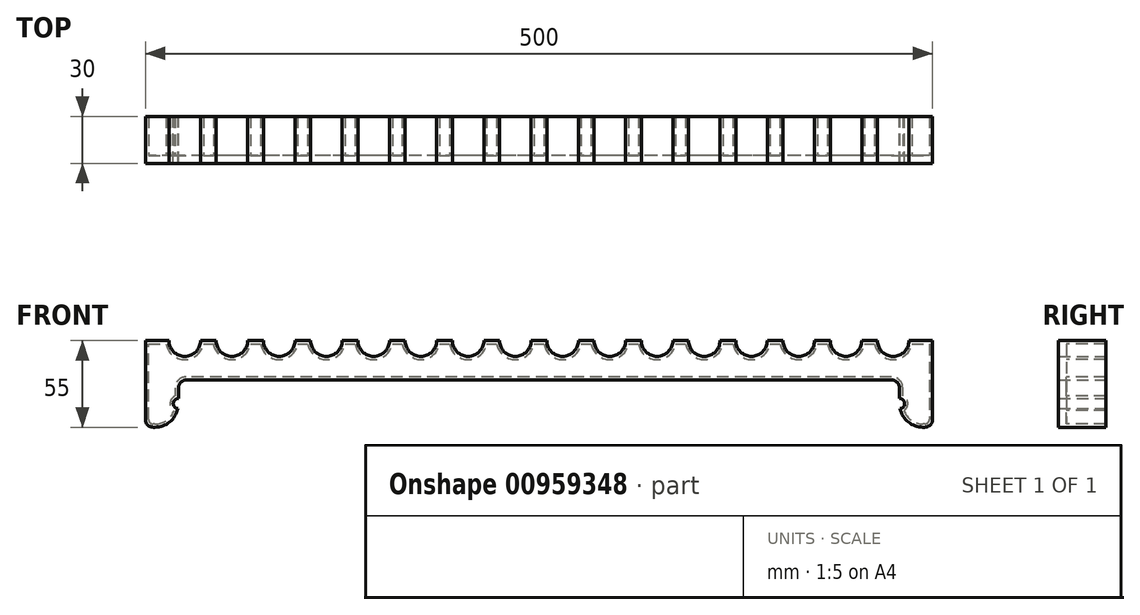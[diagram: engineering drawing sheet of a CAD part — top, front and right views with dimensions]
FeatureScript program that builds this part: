
annotation { "Feature Type Name" : "Feature", "Feature Type Description" : "" }
export const myFeature = defineFeature(function(context is Context, id is Id, definition is map)
    precondition{}
    {
        {
            var Q0;
            Q0=qCreatedBy(makeId("Front.planeOp"),FACE);
            var sketch = newSketch(context, id + "F0", { "sketchPlane" : qUnion([Q0])});
            skLineSegment(sketch, "E0.bottom", {"start": v(5, 0) * mm, "end": v(6, 0) * mm});
            skLineSegment(sketch, "E0.top", {"start": v(0, 55) * mm, "end": v(15, 55) * mm});
            skLineSegment(sketch, "E0.left", {"start": v(0, 5) * mm, "end": v(0, 55) * mm});
            skLineSegment(sketch, "E0.right", {"start": v(500, 5) * mm, "end": v(500, 55) * mm});
            skLineSegment(sketch, "E1.top", {"start": v(26, 30) * mm, "end": v(474, 30) * mm});
            skArc(sketch, "E2", {"start": v(15, 55) * mm, "mid": v(25, 45) * mm, "end": v(35, 55) * mm});
            skLineSegment(sketch, "E3.trimOffspring", {"start": v(35, 55) * mm, "end": v(45, 55) * mm});
            skLineSegment(sketch, "E4.trimOffspring", {"start": v(494, 0) * mm, "end": v(495, 0) * mm});
            skArc(sketch, "E5.1.0.0", {"start": v(45, 55) * mm, "mid": v(55, 45) * mm, "end": v(65, 55) * mm});
            skLineSegment(sketch, "E5.1.0.1", {"start": v(65, 55) * mm, "end": v(75, 55) * mm});
            skArc(sketch, "E5.2.0.0", {"start": v(75, 55) * mm, "mid": v(85, 45) * mm, "end": v(95, 55) * mm});
            skLineSegment(sketch, "E5.2.0.1", {"start": v(95, 55) * mm, "end": v(105, 55) * mm});
            skArc(sketch, "E5.3.0.0", {"start": v(105, 55) * mm, "mid": v(115, 45) * mm, "end": v(125, 55) * mm});
            skArc(sketch, "E5.4.0.0", {"start": v(135, 55) * mm, "mid": v(145, 45) * mm, "end": v(155, 55) * mm});
            skLineSegment(sketch, "E5.4.0.1", {"start": v(155, 55) * mm, "end": v(165, 55) * mm});
            skArc(sketch, "E5.5.0.0", {"start": v(165, 55) * mm, "mid": v(175, 45) * mm, "end": v(185, 55) * mm});
            skLineSegment(sketch, "E5.5.0.1", {"start": v(185, 55) * mm, "end": v(195, 55) * mm});
            skArc(sketch, "E5.6.0.0", {"start": v(195, 55) * mm, "mid": v(205, 45) * mm, "end": v(215, 55) * mm});
            skArc(sketch, "E5.7.0.0", {"start": v(225, 55) * mm, "mid": v(235, 45) * mm, "end": v(245, 55) * mm});
            skArc(sketch, "E5.8.0.0", {"start": v(255, 55) * mm, "mid": v(265, 45) * mm, "end": v(275, 55) * mm});
            skArc(sketch, "E5.9.0.0", {"start": v(285, 55) * mm, "mid": v(295, 45) * mm, "end": v(305, 55) * mm});
            skLineSegment(sketch, "E5.9.0.1", {"start": v(305, 55) * mm, "end": v(315, 55) * mm});
            skArc(sketch, "E5.10.0.0", {"start": v(315, 55) * mm, "mid": v(325, 45) * mm, "end": v(335, 55) * mm});
            skLineSegment(sketch, "E5.10.0.1", {"start": v(335, 55) * mm, "end": v(345, 55) * mm});
            skArc(sketch, "E5.11.0.0", {"start": v(345, 55) * mm, "mid": v(355, 45) * mm, "end": v(365, 55) * mm});
            skArc(sketch, "E5.12.0.0", {"start": v(375, 55) * mm, "mid": v(385, 45) * mm, "end": v(395, 55) * mm});
            skArc(sketch, "E5.13.0.0", {"start": v(405, 55) * mm, "mid": v(415, 45) * mm, "end": v(425, 55) * mm});
            skArc(sketch, "E5.14.0.0", {"start": v(435, 55) * mm, "mid": v(445, 45) * mm, "end": v(455, 55) * mm});
            skLineSegment(sketch, "E5.14.0.1", {"start": v(455, 55) * mm, "end": v(465, 55) * mm});
            skArc(sketch, "E5.15.0.0", {"start": v(465, 55) * mm, "mid": v(475, 45) * mm, "end": v(485, 55) * mm});
            skLineSegment(sketch, "E5.15.0.1", {"start": v(485, 55) * mm, "end": v(500, 55) * mm});
            skLineSegment(sketch, "E5.direction1", {"start": v(35, 55) * mm, "end": v(45, 55) * mm, "construction": true});
            skArc(sketch, "E6", {"start": v(21, 18.25) * mm, "mid": v(17.75, 15.18) * mm, "end": v(20.65, 11.77) * mm});
            skArc(sketch, "E7", {"start": v(479.35, 11.77) * mm, "mid": v(482.25, 15.18) * mm, "end": v(479, 18.25) * mm});
            skLineSegment(sketch, "E8.trimOffspring", {"start": v(125, 55) * mm, "end": v(135, 55) * mm});
            skLineSegment(sketch, "E9.trimOffspring", {"start": v(245, 55) * mm, "end": v(255, 55) * mm});
            skLineSegment(sketch, "E10.trimOffspring", {"start": v(215, 55) * mm, "end": v(225, 55) * mm});
            skLineSegment(sketch, "E11.trimOffspring", {"start": v(275, 55) * mm, "end": v(285, 55) * mm});
            skLineSegment(sketch, "E12.trimOffspring", {"start": v(425, 55) * mm, "end": v(435, 55) * mm});
            skLineSegment(sketch, "E13.trimOffspring", {"start": v(365, 55) * mm, "end": v(375, 55) * mm});
            skLineSegment(sketch, "E14.trimOffspring", {"start": v(395, 55) * mm, "end": v(405, 55) * mm});
            skLineSegment(sketch, "E15.trimOffspring", {"start": v(21, 18.25) * mm, "end": v(21, 25) * mm});
            skLineSegment(sketch, "E16.trimOffspring", {"start": v(479, 18.25) * mm, "end": v(479, 25) * mm});
            skPoint(sketch, "E17.visualSharp", {"position": v(21, 0) * mm});
            skArc(sketch, "E17.filletArc", {"start": v(6, 0) * mm, "mid": v(15.4, 3.3) * mm, "end": v(20.65, 11.77) * mm});
            skPoint(sketch, "E18.visualSharp", {"position": v(479, 0) * mm});
            skArc(sketch, "E18.filletArc", {"start": v(479.35, 11.77) * mm, "mid": v(484.6, 3.3) * mm, "end": v(494, 0) * mm});
            skPoint(sketch, "E19.visualSharp", {"position": v(21, 30) * mm});
            skArc(sketch, "E19.filletArc", {"start": v(26, 30) * mm, "mid": v(22.46, 28.54) * mm, "end": v(21, 25) * mm});
            skPoint(sketch, "E20.visualSharp", {"position": v(479, 30) * mm});
            skArc(sketch, "E20.filletArc", {"start": v(479, 25) * mm, "mid": v(477.54, 28.54) * mm, "end": v(474, 30) * mm});
            skPoint(sketch, "E21.visualSharp", {"position": v(500, 0) * mm});
            skArc(sketch, "E21.filletArc", {"start": v(495, 0) * mm, "mid": v(498.54, 1.46) * mm, "end": v(500, 5) * mm});
            skPoint(sketch, "E22.visualSharp", {"position": v(0, 0) * mm});
            skArc(sketch, "E22.filletArc", {"start": v(0, 5) * mm, "mid": v(1.46, 1.46) * mm, "end": v(5, 0) * mm});
            skSolve(sketch);
        }
        {
            var Q0;
            Q0=makeQuery(id+"F0.imprint","IMPRINT",FACE,{"disambiguationData":[TD([[makeQuery(id+"F0.imprint","IMPRINT",EDGE,{"derivedFrom":sQuery(id+"F0.wireOp",EDGE,"E0.bottom")}),1.0]])]});
            extrude(context, id + "F1", {"entities" : qUnion([Q0]), "depth" : 5 * mm, "offsetDistance" : 25 * mm});
        }
        {
            var Q0;
            Q0=makeQuery(id+"F1.opExtrude","CAP_FACE",FACE,{"disambiguationData":[OSD([sQuery(id+"F0.wireOp",EDGE,"E0.bottom"),sQuery(id+"F0.wireOp",EDGE,"E0.top"),sQuery(id+"F0.wireOp",EDGE,"E0.left"),sQuery(id+"F0.wireOp",EDGE,"E0.right"),sQuery(id+"F0.wireOp",EDGE,"E1.top"),sQuery(id+"F0.wireOp",EDGE,"E2"),sQuery(id+"F0.wireOp",EDGE,"E3.trimOffspring"),sQuery(id+"F0.wireOp",EDGE,"E4.trimOffspring"),sQuery(id+"F0.wireOp",EDGE,"E5.1.0.0"),sQuery(id+"F0.wireOp",EDGE,"E5.2.0.0"),sQuery(id+"F0.wireOp",EDGE,"E5.3.0.0"),sQuery(id+"F0.wireOp",EDGE,"E5.4.0.0"),sQuery(id+"F0.wireOp",EDGE,"E5.5.0.0"),sQuery(id+"F0.wireOp",EDGE,"E5.6.0.0"),sQuery(id+"F0.wireOp",EDGE,"E5.7.0.0"),sQuery(id+"F0.wireOp",EDGE,"E5.8.0.0"),sQuery(id+"F0.wireOp",EDGE,"E5.9.0.0"),sQuery(id+"F0.wireOp",EDGE,"E5.10.0.0"),sQuery(id+"F0.wireOp",EDGE,"E5.11.0.0"),sQuery(id+"F0.wireOp",EDGE,"E5.12.0.0"),sQuery(id+"F0.wireOp",EDGE,"E5.13.0.0"),sQuery(id+"F0.wireOp",EDGE,"E5.14.0.0"),sQuery(id+"F0.wireOp",EDGE,"E5.15.0.0"),sQuery(id+"F0.wireOp",EDGE,"E6"),sQuery(id+"F0.wireOp",EDGE,"E7"),sQuery(id+"F0.wireOp",EDGE,"E5.1.0.1"),sQuery(id+"F0.wireOp",EDGE,"E5.2.0.1"),sQuery(id+"F0.wireOp",EDGE,"E8.trimOffspring"),sQuery(id+"F0.wireOp",EDGE,"E5.4.0.1"),sQuery(id+"F0.wireOp",EDGE,"E5.5.0.1"),sQuery(id+"F0.wireOp",EDGE,"E10.trimOffspring"),sQuery(id+"F0.wireOp",EDGE,"E9.trimOffspring"),sQuery(id+"F0.wireOp",EDGE,"E11.trimOffspring"),sQuery(id+"F0.wireOp",EDGE,"E5.9.0.1"),sQuery(id+"F0.wireOp",EDGE,"E5.10.0.1"),sQuery(id+"F0.wireOp",EDGE,"E13.trimOffspring"),sQuery(id+"F0.wireOp",EDGE,"E14.trimOffspring"),sQuery(id+"F0.wireOp",EDGE,"E12.trimOffspring"),sQuery(id+"F0.wireOp",EDGE,"E5.14.0.1"),sQuery(id+"F0.wireOp",EDGE,"E5.15.0.1"),sQuery(id+"F0.wireOp",EDGE,"E15.trimOffspring"),sQuery(id+"F0.wireOp",EDGE,"E16.trimOffspring"),sQuery(id+"F0.wireOp",EDGE,"E17.filletArc"),sQuery(id+"F0.wireOp",EDGE,"E18.filletArc"),sQuery(id+"F0.wireOp",EDGE,"E19.filletArc"),sQuery(id+"F0.wireOp",EDGE,"E20.filletArc"),sQuery(id+"F0.wireOp",EDGE,"E21.filletArc"),sQuery(id+"F0.wireOp",EDGE,"E22.filletArc")])],"isStart":true});
            var sketch = newSketch(context, id + "F2", { "sketchPlane" : qUnion([Q0])});
            skLineSegment(sketch, "E23.0", {"start": v(-336.83, 53) * mm, "end": v(-343.17, 53) * mm});
            skArc(sketch, "E23.1", {"start": v(-313.17, 53) * mm, "mid": v(-325, 43) * mm, "end": v(-336.83, 53) * mm});
            skArc(sketch, "E23.2", {"start": v(-18.21, 10.55) * mm, "mid": v(-13.45, 4.35) * mm, "end": v(-6, 2) * mm});
            skArc(sketch, "E23.3", {"start": v(-19, 19.85) * mm, "mid": v(-15.77, 15.44) * mm, "end": v(-18.21, 10.55) * mm});
            skLineSegment(sketch, "E23.4", {"start": v(-19, 25) * mm, "end": v(-19, 19.85) * mm});
            skArc(sketch, "E23.5", {"start": v(-26, 32) * mm, "mid": v(-21.05, 29.95) * mm, "end": v(-19, 25) * mm});
            skLineSegment(sketch, "E23.6", {"start": v(-474, 32) * mm, "end": v(-26, 32) * mm});
            skArc(sketch, "E23.7", {"start": v(-481, 25) * mm, "mid": v(-478.95, 29.95) * mm, "end": v(-474, 32) * mm});
            skLineSegment(sketch, "E23.8", {"start": v(-481, 19.85) * mm, "end": v(-481, 25) * mm});
            skArc(sketch, "E23.9", {"start": v(-481.79, 10.55) * mm, "mid": v(-484.23, 15.44) * mm, "end": v(-481, 19.85) * mm});
            skArc(sketch, "E23.10", {"start": v(-494, 2) * mm, "mid": v(-486.55, 4.35) * mm, "end": v(-481.79, 10.55) * mm});
            skLineSegment(sketch, "E23.11", {"start": v(-495, 2) * mm, "end": v(-494, 2) * mm});
            skArc(sketch, "E23.12", {"start": v(-498, 5) * mm, "mid": v(-497.12, 2.88) * mm, "end": v(-495, 2) * mm});
            skLineSegment(sketch, "E23.13", {"start": v(-498, 53) * mm, "end": v(-498, 5) * mm});
            skLineSegment(sketch, "E23.14", {"start": v(-396.83, 53) * mm, "end": v(-403.17, 53) * mm});
            skArc(sketch, "E23.15", {"start": v(-373.17, 53) * mm, "mid": v(-385, 43) * mm, "end": v(-396.83, 53) * mm});
            skLineSegment(sketch, "E23.16", {"start": v(-366.83, 53) * mm, "end": v(-373.17, 53) * mm});
            skArc(sketch, "E23.17", {"start": v(-343.17, 53) * mm, "mid": v(-355, 43) * mm, "end": v(-366.83, 53) * mm});
            skArc(sketch, "E23.18", {"start": v(-403.17, 53) * mm, "mid": v(-415, 43) * mm, "end": v(-426.83, 53) * mm});
            skLineSegment(sketch, "E23.19", {"start": v(-426.83, 53) * mm, "end": v(-433.17, 53) * mm});
            skArc(sketch, "E23.20", {"start": v(-433.17, 53) * mm, "mid": v(-445, 43) * mm, "end": v(-456.83, 53) * mm});
            skLineSegment(sketch, "E23.21", {"start": v(-456.83, 53) * mm, "end": v(-463.17, 53) * mm});
            skArc(sketch, "E23.22", {"start": v(-463.17, 53) * mm, "mid": v(-475, 43) * mm, "end": v(-486.83, 53) * mm});
            skLineSegment(sketch, "E23.23", {"start": v(-486.83, 53) * mm, "end": v(-498, 53) * mm});
            skLineSegment(sketch, "E23.24", {"start": v(-6, 2) * mm, "end": v(-5, 2) * mm});
            skArc(sketch, "E23.25", {"start": v(-5, 2) * mm, "mid": v(-2.88, 2.88) * mm, "end": v(-2, 5) * mm});
            skLineSegment(sketch, "E23.26", {"start": v(-2, 5) * mm, "end": v(-2, 53) * mm});
            skLineSegment(sketch, "E23.27", {"start": v(-2, 53) * mm, "end": v(-13.17, 53) * mm});
            skArc(sketch, "E23.28", {"start": v(-13.17, 53) * mm, "mid": v(-25, 43) * mm, "end": v(-36.83, 53) * mm});
            skLineSegment(sketch, "E23.29", {"start": v(-36.83, 53) * mm, "end": v(-43.17, 53) * mm});
            skArc(sketch, "E23.30", {"start": v(-43.17, 53) * mm, "mid": v(-55, 43) * mm, "end": v(-66.83, 53) * mm});
            skLineSegment(sketch, "E23.31", {"start": v(-66.83, 53) * mm, "end": v(-73.17, 53) * mm});
            skArc(sketch, "E23.32", {"start": v(-73.17, 53) * mm, "mid": v(-85, 43) * mm, "end": v(-96.83, 53) * mm});
            skLineSegment(sketch, "E23.33", {"start": v(-96.83, 53) * mm, "end": v(-103.17, 53) * mm});
            skArc(sketch, "E23.34", {"start": v(-103.17, 53) * mm, "mid": v(-115, 43) * mm, "end": v(-126.83, 53) * mm});
            skLineSegment(sketch, "E23.35", {"start": v(-126.83, 53) * mm, "end": v(-133.17, 53) * mm});
            skArc(sketch, "E23.36", {"start": v(-133.17, 53) * mm, "mid": v(-145, 43) * mm, "end": v(-156.83, 53) * mm});
            skLineSegment(sketch, "E23.37", {"start": v(-156.83, 53) * mm, "end": v(-163.17, 53) * mm});
            skArc(sketch, "E23.38", {"start": v(-163.17, 53) * mm, "mid": v(-175, 43) * mm, "end": v(-186.83, 53) * mm});
            skLineSegment(sketch, "E23.39", {"start": v(-186.83, 53) * mm, "end": v(-193.17, 53) * mm});
            skArc(sketch, "E23.40", {"start": v(-193.17, 53) * mm, "mid": v(-205, 43) * mm, "end": v(-216.83, 53) * mm});
            skLineSegment(sketch, "E23.41", {"start": v(-216.83, 53) * mm, "end": v(-223.17, 53) * mm});
            skArc(sketch, "E23.42", {"start": v(-223.17, 53) * mm, "mid": v(-235, 43) * mm, "end": v(-246.83, 53) * mm});
            skLineSegment(sketch, "E23.43", {"start": v(-246.83, 53) * mm, "end": v(-253.17, 53) * mm});
            skArc(sketch, "E23.44", {"start": v(-253.17, 53) * mm, "mid": v(-265, 43) * mm, "end": v(-276.83, 53) * mm});
            skLineSegment(sketch, "E23.45", {"start": v(-276.83, 53) * mm, "end": v(-283.17, 53) * mm});
            skArc(sketch, "E23.46", {"start": v(-283.17, 53) * mm, "mid": v(-295, 43) * mm, "end": v(-306.83, 53) * mm});
            skLineSegment(sketch, "E23.47", {"start": v(-306.83, 53) * mm, "end": v(-313.17, 53) * mm});
            skSolve(sketch);
        }
        {
            var Q0;
            Q0=makeQuery(id+"F2.imprint","IMPRINT",FACE,{"disambiguationData":[TD([[makeQuery(id+"F2.imprint","IMPRINT",EDGE,{"derivedFrom":sQuery(id+"F2.wireOp",EDGE,"E23.0")}),-1.0]])]});
            extrude(context, id + "F3", {"entities" : qUnion([Q0]), "operationType" : NewBodyOperationType.ADD, "depth" : 25 * mm, "offsetDistance" : 25 * mm});
        }
    });
